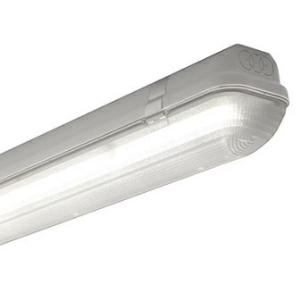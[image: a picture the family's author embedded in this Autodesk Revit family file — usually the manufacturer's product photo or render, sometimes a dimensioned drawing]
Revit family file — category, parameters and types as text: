
# Revit family: 3f_filippi_-_3f_linda_3f_filippi_-_58713_-_3f_linda_led_1x24w_enp_l1270
name_source: partatom
category: Lighting Fixtures
units: mm (PartAtom-declared; Revit-internal decimal feet)

## family parameters
Cut with Voids When Loaded = No
Host = Face
Light Source = No
Part Type = Normal
Room Calculation Point = No
Round Connector Dimension = Use Diameter
Shared = No

## types (1)
- 3F Filippi - 3F Linda (1 x LED, 544 lm, 1 W, 4000 K)
    Apparent Load = 1 VA
    Approval mark = ENEC
    CIE Flux Codes = 44 77 94 97 100
    Color Rendering = 80
    Color Temperature = 4000 K
    Default Elevation = 1800 mm
    Description = ILLUMINOTECHNICAL
Luminous efficiency 100% (DLOR 97%, ULOR 3%).
Emergency luminaire luminous flux 544 lm.
Controlled symmetric distribution.
Installation Interdistance Transv.D = 1.77 x hu - Long.D = 1.17 x hu.
Tabular UGR (CIE 117 - 4H-8H; S=0.25H; 70/50/20): RUG 15 - 15.9.
Beam angle: 109° - 64°.
Lifetime (L93/B10): 30000 h. (tq+25°C)
Lifetime (L90/B10): 50000 h. (tq+25°C)
Sudden decreased luminous flux after 50000 hours: 0% (C0).
Photobiological safety in compliance with IEC/TR 62778: RG0 risk exempt, (IEC 62471).
In compliance with IEC/EN 62722-2-1 - IEC/EN 62717 standards.

SOURCE
Linear LED module 24W/840.
Energy efficiency class (UE 2019/2020 - UE 2019/2015): D.
CIE 13.3 Colour rendering index: CRI >80 (R9 <50%).
IES TM-30 Fidelity Index: Rf = 84 Rg = 95.
CCT nominal colour temperature 4000 K.
Colour initial tolerance (MacAdam): SDCM 3.

MECHANICAL
Self-extinguishing V2 polycarbonate housing, injection moulded, RAL 7035 grey.
Ecologic anti-aging injected sealing gasket.
Diffuser in self-extinguishing V2 polycarbonate, photo-engraved interior, UV stabilised, injection moulded with smooth outer surface, tamper-proof opening.
Gear-holder reflector in hot-dip galvanised steel, painted with white polyester base.
Snug fit safety snap-lock clips for diffuser mounting in stainless steel, screwdriver opening.
Fixing brackets in stainless steel.
Possibility for technicians to access the interior of the luminaire.
Luminaire with limited surface temperature. - D - (EN 60598-2-24)
Dimensions: 1270x100 mm, height 100 mm. Weight 2.195 kg.
IP66 protection degree.
Mechanical strength to impacts IK10 (20 joule).
Glow-wire test resistance 850°C.

ELECTRICAL
Power of the luminaire 1 W.
CE - IEC 60598-1 - EN 60598-1.
ENP non-permanent emergency wiring, 1h duration, 24h recharge; compliant with EN 60598-2-22, excluding high risk areas.
SAFE FLICKER: PstLM=<1 and SVM=<0.4 (IEC TR 61547-1 and IEC TR 63158), to ensure a more comfortable and safe light.
Ambient temperature from +5°C to +25°C.
Temperature class T6 max 85°C.
Relative humidity UR: <85%.

INSTALLATION
Ceiling / Suspended / Wall.
All accessories dedicated to this product are available on the Catalog and on our website www.3F-Filippi.com.

APPLICATIONS
Suitable product for food production plants (HACCP), IFS (Food Version 6), BRC (GSFS Food Version 7).
Dry, dusty indoor environments, subject to occasional water splashes.
Virtually shatterproof polycarbonate compatibly with the fumes / atmospheres that compromise the elasticity of plastic materials.
Not suitable for installation on surfaces subject to important vibrations, exposed to weather conditions, on ropes or poles.
Suitable for illumination of public car parks and parking grounds referred to DIN 67528:2018-04.

WARNING
Fixture not suitable for cold stores with an ambient temperature <5°C and/or relative humidity >85%.
Luminaire designed for disposal/recycling at end-of-life.
Replaceable (LED only) light source by a professional. Replaceable control gear by a professional.
    Height = 100 mm  [stored 0.328084 ft]
    Lamp = 1 x LED
    Lamp Light Flux = 544 lm
    Lamp Power = 1 W
    Lamp count = 1
    Length = 1270 mm
    Lifetime = 50000 h
    Luminous efficacy = 544 lm/W
    Manufacturer = 3F Filippi
    ModVariant = No
    Model = 3F Filippi - 58713 - 3F Linda LED 1x24W ENP L1270
    Mounting Place = Ceiling
    Mounting Type = Pendant
    Number of Poles = 1
    OnlyDefault = Yes
    Power Factor = 1
    Product Name = 3F Filippi - 3F Linda
    Product group = pendant luminaire
    ProductGroupID = 9
    Protection Class = Protection class I
    Protection Degree = IP 66
    RLX_Detail_Level = 1
    RLX_Emergency_Light_Flux = 0 lm
    RLX_Emergency_Type = 0
    RLX_Emergency_Type_DB = No
    RlxData = <blob elided: 67857 chars, md5=2bb5ff21>
    Socket = socket
    Standby Power = 0 W
    System Light Flux = 544 lm
    System Power = 1 W
    Type Comments = Product without accessories
    Type Image = 3ffilippi_58713.jpg
    URL = http://relux.com
    VarID = ---
    Voltage = 0 V
    Weight = 0.00 kg
    Width = 100 mm  [stored 0.328084 ft]

note: [stored X ft] marks values corroborated as IEEE doubles in the binary element streams (Revit-internal decimal feet)

## geometry (parser evidence)
native form markers: Blend x4, Sweep x10
no freeform markers — native parametric forms only
